# Revit family: Vitocrossal 300 CA3B 6.0 Dual Fuel With Combustion Air Intake
name_source: partatom
category: Mechanical Equipment
units: mm (PartAtom-declared; Revit-internal decimal feet)

## family parameters
Always vertical = Yes
Classification = None
Cut with Voids When Loaded = No
OmniClass Number = 23.75.10.11.14.14
OmniClass Title = Condensing Boilers
Part Type = Normal
Room Calculation Point = No
Round Connector Dimension = Use Diameter
Shared = No
Work Plane-Based = No

## types (1)
- Standard
    Connector_1_Diameter = 0' - 6"
    Connector_2_Diameter = 0' - 6"
    Connector_3_Diameter = 0' - 2"
    Connector_4_Diameter = 0' - 3"
    Connector_5_Diameter = 1' - 4"
    Connector_6_Diameter = 1' - 4"
    Description = Dual Fuel Commercial Condensing Boiler
    Manufacturer = Viessmann
    Model = Vitocrossal 300 CA3B 6.0 Dual Fuel With Combustion Air Intake
    URL = www.viessmann.ca

## geometry (parser evidence)
native form markers: Sweep x2
no freeform markers — native parametric forms only
